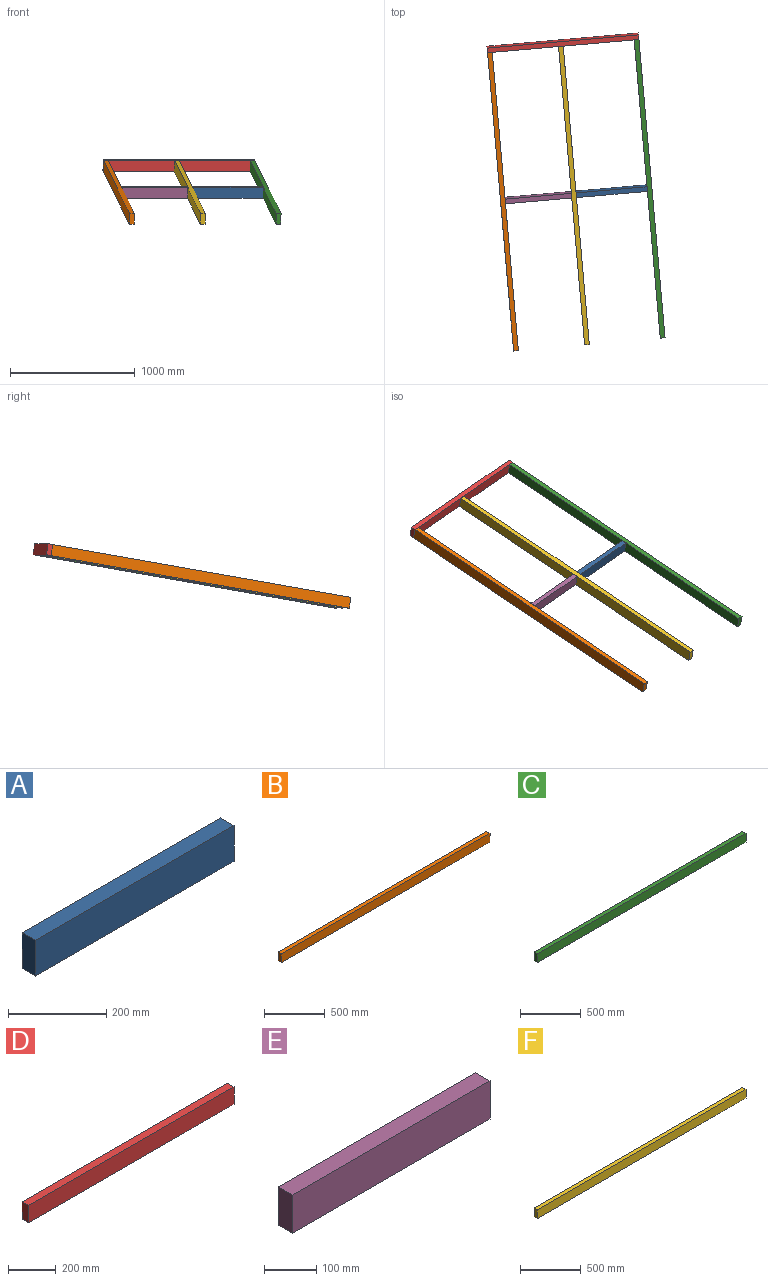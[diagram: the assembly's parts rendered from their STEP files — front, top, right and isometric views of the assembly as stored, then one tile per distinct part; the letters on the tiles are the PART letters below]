
ASSEMBLY  parts=6 mates=5
PART A: 6 faces, bbox 571.5x38.1x88.9 mm
  f0: plane 571.5x38.1mm, normal (0,0,1), area 21774.1mm2, adj f1,f3,f4,f5
  f1: plane 88.9x38.1mm, normal (-1,0,0), area 3387.1mm2, adj f0,f2,f4,f5
  f2: plane 571.5x38.1mm, normal (0,0,-1), area 21774.1mm2, adj f1,f3,f4,f5
  f3: plane 88.9x38.1mm, normal (1,0,0), area 3387.1mm2, adj f0,f2,f4,f5
  f4: plane 571.5x88.9mm, normal (0,-1,0), area 50806.3mm2, adj f0,f1,f2,f3
  f5: plane 571.5x88.9mm, normal (0,1,0), area 50806.3mm2, adj f0,f1,f2,f3
PART B: 6 faces, bbox 2438.4x38.1x88.9 mm
  f0: plane 2438.4x38.1mm, normal (0,0,-1), area 92903mm2, adj f1,f3,f4,f5
  f1: plane 88.9x38.1mm, normal (1,0,0), area 3387.1mm2, adj f0,f2,f4,f5
  f2: plane 2438.4x38.1mm, normal (0,0,1), area 92903mm2, adj f1,f3,f4,f5
  f3: plane 88.9x38.1mm, normal (-1,0,0), area 3387.1mm2, adj f0,f2,f4,f5
  f4: plane 2438.4x88.9mm, normal (0,-1,0), area 216773.8mm2, adj f0,f1,f2,f3
  f5: plane 2438.4x88.9mm, normal (0,1,0), area 216773.8mm2, adj f0,f1,f2,f3
PART C: 6 faces, bbox 2438.4x38.1x88.9 mm
  f0: plane 2438.4x38.1mm, normal (0,0,1), area 92903mm2, adj f1,f3,f4,f5
  f1: plane 88.9x38.1mm, normal (-1,0,0), area 3387.1mm2, adj f0,f2,f4,f5
  f2: plane 2438.4x38.1mm, normal (0,0,-1), area 92903mm2, adj f1,f3,f4,f5
  f3: plane 88.9x38.1mm, normal (1,0,0), area 3387.1mm2, adj f0,f2,f4,f5
  f4: plane 2438.4x88.9mm, normal (0,-1,0), area 216773.8mm2, adj f0,f1,f2,f3
  f5: plane 2438.4x88.9mm, normal (0,1,0), area 216773.8mm2, adj f0,f1,f2,f3
PART D: 6 faces, bbox 1219.2x38.1x88.9 mm
  f0: plane 1219.2x38.1mm, normal (0,0,-1), area 46451.5mm2, adj f1,f3,f4,f5
  f1: plane 88.9x38.1mm, normal (1,0,0), area 3387.1mm2, adj f0,f2,f4,f5
  f2: plane 1219.2x38.1mm, normal (0,0,1), area 46451.5mm2, adj f1,f3,f4,f5
  f3: plane 88.9x38.1mm, normal (-1,0,0), area 3387.1mm2, adj f0,f2,f4,f5
  f4: plane 1219.2x88.9mm, normal (0,-1,0), area 108386.9mm2, adj f0,f1,f2,f3
  f5: plane 1219.2x88.9mm, normal (0,1,0), area 108386.9mm2, adj f0,f1,f2,f3
PART E: 6 faces, bbox 533.4x38.1x88.9 mm
  f0: plane 88.9x38.1mm, normal (-1,0,0), area 3387.1mm2, adj f1,f3,f4,f5
  f1: plane 533.4x38.1mm, normal (0,0,-1), area 20322.5mm2, adj f0,f2,f4,f5
  f2: plane 88.9x38.1mm, normal (1,0,0), area 3387.1mm2, adj f1,f3,f4,f5
  f3: plane 533.4x38.1mm, normal (0,0,1), area 20322.5mm2, adj f0,f2,f4,f5
  f4: plane 533.4x88.9mm, normal (0,-1,0), area 47419.3mm2, adj f0,f1,f2,f3
  f5: plane 533.4x88.9mm, normal (0,1,0), area 47419.3mm2, adj f0,f1,f2,f3
PART F: 6 faces, bbox 2438.4x38.1x88.9 mm
  f0: plane 88.9x38.1mm, normal (-1,0,0), area 3387.1mm2, adj f1,f3,f4,f5
  f1: plane 2438.4x38.1mm, normal (0,0,-1), area 92903mm2, adj f0,f2,f4,f5
  f2: plane 88.9x38.1mm, normal (1,0,0), area 3387.1mm2, adj f1,f3,f4,f5
  f3: plane 2438.4x38.1mm, normal (0,0,1), area 92903mm2, adj f0,f2,f4,f5
  f4: plane 2438.4x88.9mm, normal (0,-1,0), area 216773.8mm2, adj f0,f1,f2,f3
  f5: plane 2438.4x88.9mm, normal (0,1,0), area 216773.8mm2, adj f0,f1,f2,f3
PLACE A rot(axis=(0.89,0.04,0.45),11.2deg) t=(455.49,-1194.21,-356.82)mm
PLACE B rot(axis=(0.09,0.09,-0.99),85.5deg) t=(-382.38,-2471.58,-685)mm
PLACE C rot(axis=(0.09,0.09,-0.99),85.5deg) t=(685.11,-1121.47,-211.49)mm
PLACE D rot(axis=(-1,-0.04,0),170deg) t=(38.99,-40.18,-171.18)mm fixed
PLACE E rot(axis=(0.89,0.04,0.45),11.2deg) t=(350.13,-1197.05,-392.86)mm
PLACE F rot(axis=(0.09,0.09,-0.99),85.5deg) t=(81.71,-1218.96,-280.94)mm
MATE fastened C.f4 <-> A.f3  axis (-1,-0.09,0) through (653.48,-1197.09,-352.39)mm
MATE fastened F.f0 <-> D.f5  axis (-0.09,0.98,0.17) through (-21.16,-43.1,-184.46)mm
MATE fastened B.f0 <-> D.f2  axis (-0.02,0.17,-0.98) through (-628.44,-96.23,-184.46)mm
MATE fastened C.f1 <-> D.f5  axis (-0.09,0.98,0.17) through (587.46,-5.35,-96.91)mm
MATE fastened B.f5 <-> E.f0  axis (1,0.09,0) through (-484.5,-1304.39,-308.62)mm
